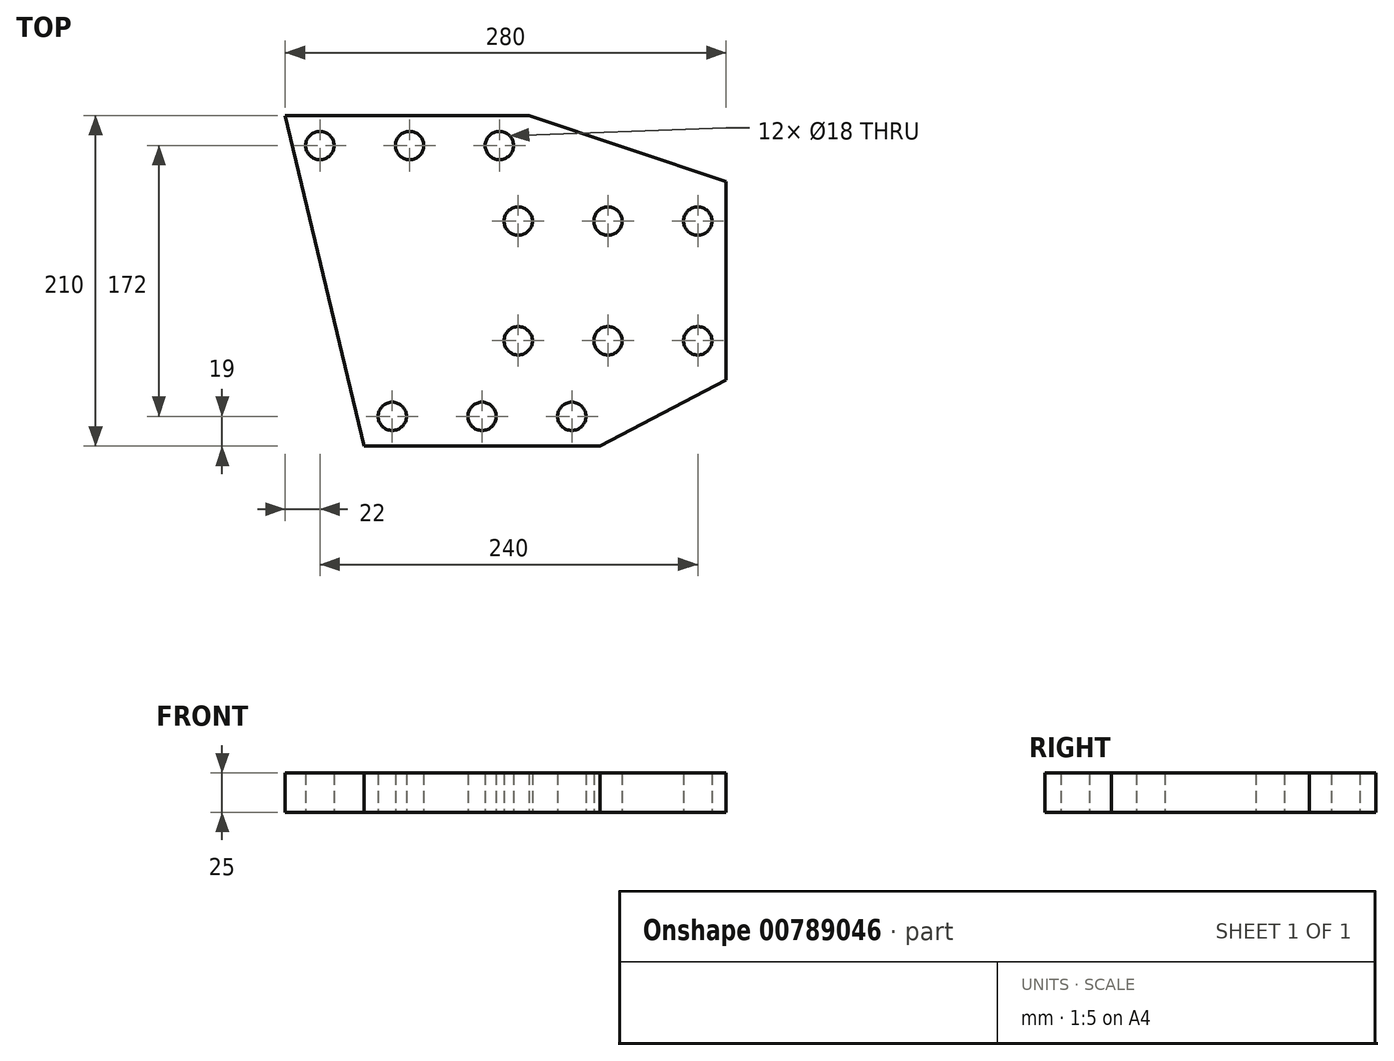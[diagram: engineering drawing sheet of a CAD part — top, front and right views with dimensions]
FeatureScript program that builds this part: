
annotation { "Feature Type Name" : "Feature", "Feature Type Description" : "" }
export const myFeature = defineFeature(function(context is Context, id is Id, definition is map)
    precondition{}
    {
        {
            var Q0;
            Q0=qCreatedBy(makeId("Top.planeOp"),FACE);
            var sketch = newSketch(context, id + "F0", { "sketchPlane" : qUnion([Q0])});
            skLineSegment(sketch, "E0.bottom", {"start": v(-80, 0) * mm, "end": v(-230, 0) * mm});
            skLineSegment(sketch, "E0.top", {"start": v(-125, 210) * mm, "end": v(-280, 210) * mm});
            skLineSegment(sketch, "E0.left", {"start": v(0, 42) * mm, "end": v(0, 168) * mm});
            skPoint(sketch, "E1", {"position": v(0, 42) * mm});
            skPoint(sketch, "E2", {"position": v(-80, 0) * mm});
            skPoint(sketch, "E3", {"position": v(-125, 210) * mm});
            skPoint(sketch, "E4", {"position": v(0, 168) * mm});
            skPoint(sketch, "E5", {"position": v(-230, 0) * mm});
            skLineSegment(sketch, "E6", {"start": v(-280, 210) * mm, "end": v(-230, 0) * mm});
            skLineSegment(sketch, "E7", {"start": v(-80, 0) * mm, "end": v(0, 42) * mm});
            skLineSegment(sketch, "E8", {"start": v(0, 168) * mm, "end": v(-125, 210) * mm});
            skCircle(sketch, "E9", {"center": v(-18, 143) * mm, "radius": 9 * mm});
            skCircle(sketch, "E10", {"center": v(-18, 67) * mm, "radius": 9 * mm});
            skCircle(sketch, "E11", {"center": v(-75, 143) * mm, "radius": 9 * mm});
            skCircle(sketch, "E12", {"center": v(-75, 67) * mm, "radius": 9 * mm});
            skCircle(sketch, "E13", {"center": v(-132, 67) * mm, "radius": 9 * mm});
            skCircle(sketch, "E14", {"center": v(-132, 143) * mm, "radius": 9 * mm});
            skCircle(sketch, "E15", {"center": v(-258, 191) * mm, "radius": 9 * mm});
            skCircle(sketch, "E16", {"center": v(-201, 191) * mm, "radius": 9 * mm});
            skCircle(sketch, "E17", {"center": v(-144, 191) * mm, "radius": 9 * mm});
            skCircle(sketch, "E18", {"center": v(-212, 19) * mm, "radius": 9 * mm});
            skCircle(sketch, "E19", {"center": v(-155, 19) * mm, "radius": 9 * mm});
            skCircle(sketch, "E20", {"center": v(-98, 19) * mm, "radius": 9 * mm});
            skPoint(sketch, "E21.orphan", {"position": v(0, 0) * mm});
            skPoint(sketch, "E22.orphan", {"position": v(0, 210) * mm});
            skSolve(sketch);
        }
        {
            var Q0;
            Q0 = qSketchRegion(id + "F0", true);
            extrude(context, id + "F1", {"entities" : qUnion([Q0]), "depth" : 25 * mm, "offsetDistance" : 25 * mm});
        }
    });
